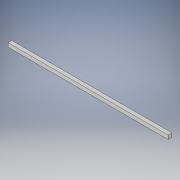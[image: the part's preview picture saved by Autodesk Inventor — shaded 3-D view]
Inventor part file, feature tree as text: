
AUTODESK INVENTOR PART (.ipt)
format: ipt  version: 2017 (Build 210142000, 142)  size: 91,648 bytes
history: native  units: in
note: dims shown in document units (in); Inventor stores cm internally (conversion verified against a paired STEP export)
features: extrude x1, sketch x1
ambient origin geometry x8: Origin, YZ Plane, XZ Plane, XY Plane, X Axis, Y Axis, Z Axis, Center Point
bodies: Solid1 (feature_tree)
feature tree (2):
  extrude  "Extrusion1"  Depth=0.25in
  sketch  "Sketch1"  dims[d0=10.5in d1=0.25in d2=0.25in d3=0.0in]
